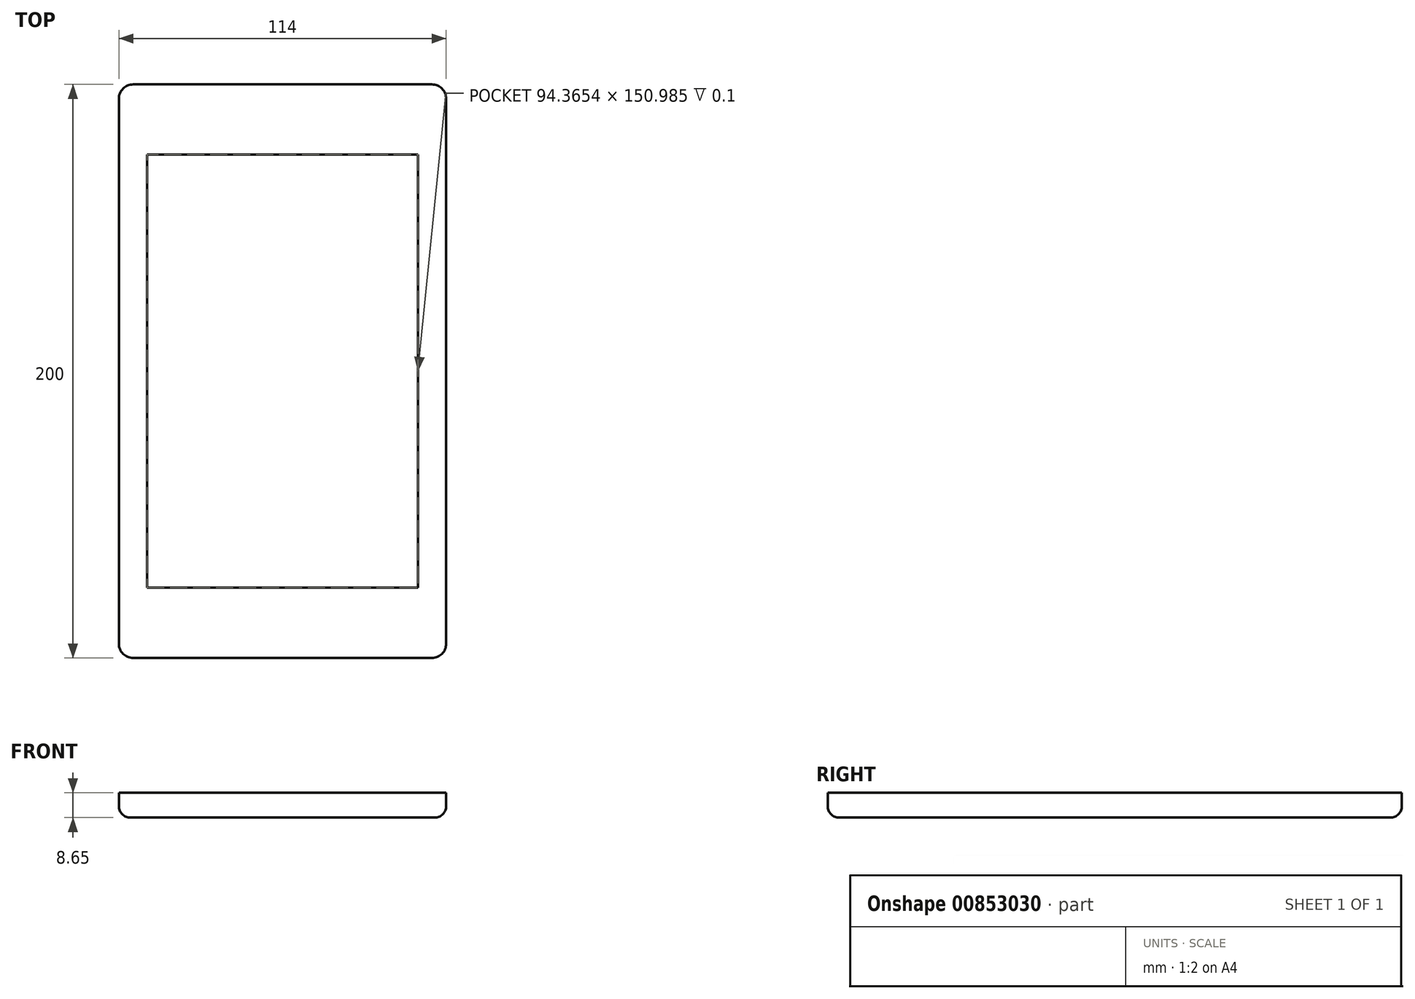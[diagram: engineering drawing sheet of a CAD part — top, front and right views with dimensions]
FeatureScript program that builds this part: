
annotation { "Feature Type Name" : "Feature", "Feature Type Description" : "" }
export const myFeature = defineFeature(function(context is Context, id is Id, definition is map)
    precondition{}
    {
        {
            assignVariable(context, id + "F0", {"name" : "T", "anyValue" : 8.65});
        }
        {
            var Q0;
            Q0=qCreatedBy(makeId("Top.planeOp"),FACE);
            var sketch = newSketch(context, id + "F1", { "sketchPlane" : qUnion([Q0])});
            skLineSegment(sketch, "E0.bottom", {"start": v(57, -100) * mm, "end": v(-57, -100) * mm});
            skLineSegment(sketch, "E0.top", {"start": v(57, 100) * mm, "end": v(-57, 100) * mm});
            skLineSegment(sketch, "E0.left", {"start": v(57, -100) * mm, "end": v(57, 100) * mm});
            skLineSegment(sketch, "E0.right", {"start": v(-57, -100) * mm, "end": v(-57, 100) * mm});
            skPoint(sketch, "E0.middle", {"position": v(0, 0) * mm});
            skSolve(sketch);
        }
        {
            var Q0;
            Q0=makeQuery(id+"F1.imprint","IMPRINT",FACE,{"disambiguationData":[TD([[makeQuery(id+"F1.imprint","IMPRINT",EDGE,{"derivedFrom":sQuery(id+"F1.wireOp",EDGE,"E0.bottom")}),-1.0]])]});
            extrude(context, id + "F2", {"entities" : qUnion([Q0]), "depth" : (getVariable(context, 'T')) * mm, "offsetDistance" : 25 * mm});
        }
        {
            var Q0;
            Q0=makeQuery(id+"F2.opExtrude","CAP_FACE",FACE,{"disambiguationData":[OSD([sQuery(id+"F1.wireOp",EDGE,"E0.bottom"),sQuery(id+"F1.wireOp",EDGE,"E0.top"),sQuery(id+"F1.wireOp",EDGE,"E0.left"),sQuery(id+"F1.wireOp",EDGE,"E0.right")])],"isStart":false});
            var sketch = newSketch(context, id + "F3", { "sketchPlane" : qUnion([Q0])});
            skLineSegment(sketch, "E1.bottom", {"start": v(47.18, -75.5) * mm, "end": v(-47.18, -75.5) * mm});
            skLineSegment(sketch, "E1.top", {"start": v(47.18, 75.5) * mm, "end": v(-47.18, 75.5) * mm});
            skLineSegment(sketch, "E1.left", {"start": v(47.18, -75.5) * mm, "end": v(47.18, 75.5) * mm});
            skLineSegment(sketch, "E1.right", {"start": v(-47.18, -75.5) * mm, "end": v(-47.18, 75.5) * mm});
            skPoint(sketch, "E1.middle", {"position": v(0, 0) * mm});
            skSolve(sketch);
        }
        {
            var Q0;
            Q0 = qSketchRegion(id + "F3", true);
            extrude(context, id + "F4", {"entities" : qUnion([Q0]), "operationType" : NewBodyOperationType.REMOVE, "oppositeDirection" : true, "depth" : 0.1 * mm, "offsetDistance" : 25 * mm});
        }
        {
            var Q0;
            Q0=makeQuery(id+"F2.opExtrude","SWEPT_EDGE",EDGE,{"disambiguationData":[OSD([sQuery(id+"F1.wireOp",EDGE,"E0.bottom"),sQuery(id+"F1.wireOp",EDGE,"E0.right")])]});
            var Q1;
            Q1=makeQuery(id+"F2.opExtrude","SWEPT_EDGE",EDGE,{"disambiguationData":[OSD([sQuery(id+"F1.wireOp",EDGE,"E0.bottom"),sQuery(id+"F1.wireOp",EDGE,"E0.left")])]});
            var Q2;
            Q2=makeQuery(id+"F2.opExtrude","SWEPT_EDGE",EDGE,{"disambiguationData":[OSD([sQuery(id+"F1.wireOp",EDGE,"E0.top"),sQuery(id+"F1.wireOp",EDGE,"E0.right")])]});
            var Q3;
            Q3=makeQuery(id+"F2.opExtrude","SWEPT_EDGE",EDGE,{"disambiguationData":[OSD([sQuery(id+"F1.wireOp",EDGE,"E0.top"),sQuery(id+"F1.wireOp",EDGE,"E0.left")])]});
            fillet(context, id + "F5", {"entities" : qUnion([Q0, Q1, Q2, Q3]), "radius" : 5 * mm, "tangentPropagation" : true, "allowEdgeOverflow" : false});
        }
        {
            var Q0;
            Q0=makeQuery(id+"F2.opExtrude","CAP_EDGE",EDGE,{"disambiguationData":[OSD([sQuery(id+"F1.wireOp",EDGE,"E0.right")])],"isStart":true});
            fillet(context, id + "F6", {"entities" : qUnion([Q0]), "radius" : 4 * mm, "tangentPropagation" : true, "allowEdgeOverflow" : false});
        }
    });
